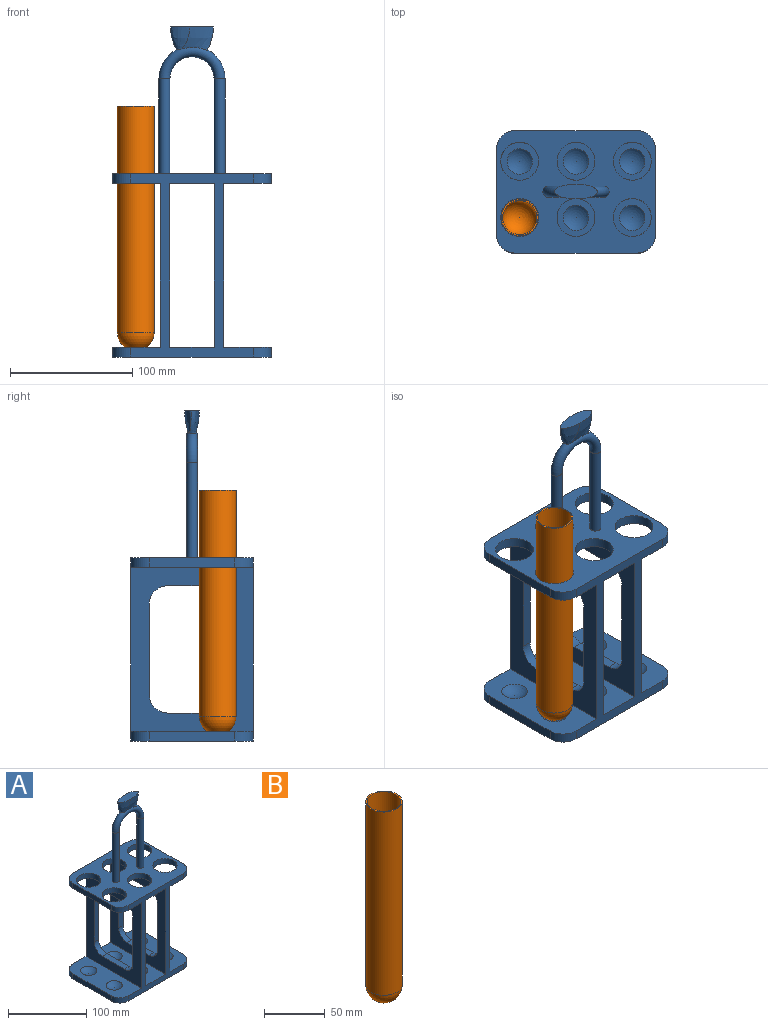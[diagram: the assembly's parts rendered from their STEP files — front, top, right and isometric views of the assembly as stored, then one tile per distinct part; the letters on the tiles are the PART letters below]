
ASSEMBLY  parts=2 mates=1
PART A: 62 faces, bbox 130.6x100.6x270.6 mm
  f0: plane 130x100mm, normal (0,0,1), area 8151mm2, adj f1,f3,f5,f7,f9,f15,f16,f26
  f1: cylinder r=15.5mm len=31mm, axis (0,0,-1), area 779.1mm2, adj f0,f25
  f2: sphere r=15.5mm, area 389.6mm2, adj f22
  f3: cylinder r=15.5mm len=31mm, axis (0,0,-1), area 779.1mm2, adj f0,f23
  f4: sphere r=15.5mm, area 389.6mm2, adj f24
  f5: cylinder r=15.5mm len=31mm, axis (0,0,-1), area 779.1mm2, adj f0,f17
  f6: sphere r=15.5mm, area 389.6mm2, adj f18
  f7: cylinder r=15.5mm len=31mm, axis (0,0,-1), area 779.1mm2, adj f0,f25
  f8: sphere r=15.5mm, area 389.6mm2, adj f22
  f9: cylinder r=15.5mm len=31mm, axis (0,0,-1), area 779.1mm2, adj f0,f23
  f10: sphere r=15.5mm, area 389.6mm2, adj f24
  f11: plane 134x100mm, normal (-1,0,0), area 6313.1mm2, adj f17,f18,f26,f27,f28,f29,f30,f31
  f12: plane 134x100mm, normal (1,0,0), area 6313.1mm2, adj f22,f25,f26,f27,f36,f37,f38,f39
  f13: plane 134x100mm, normal (-1,0,0), area 6313.1mm2, adj f23,f24,f26,f27,f36,f37,f38,f39
  f14: plane 134x100mm, normal (1,0,0), area 6313.1mm2, adj f23,f24,f26,f27,f28,f29,f30,f31
  f15: plane 70x8mm, normal (1,0,0), area 560mm2, adj f0,f25,f46,f50
  f16: plane 70x8mm, normal (-1,0,0), area 560mm2, adj f0,f17,f49,f53
  f17: plane 100x39mm, normal (0,0,-1), area 2293.9mm2, adj f5,f11,f16,f26,f27,f45,f49,f53
  f18: plane 100x39mm, normal (0,0,1), area 3124.8mm2, adj f6,f11,f19,f26,f27,f44,f48,f52
  f19: plane 70x8mm, normal (-1,0,0), area 560mm2, adj f18,f20,f48,f52
  f20: plane 130x100mm, normal (0,0,-1), area 12806.9mm2, adj f19,f21,f26,f27,f47,f48,f51,f52
  f21: plane 70x8mm, normal (1,0,0), area 560mm2, adj f20,f22,f47,f51
  f22: plane 100x39mm, normal (0,0,1), area 3124.8mm2, adj f2,f8,f12,f21,f26,f27,f47,f51
  f23: plane 100x36mm, normal (0,0,-1), area 2090.5mm2, adj f3,f9,f13,f14,f26,f27
  f24: plane 100x36mm, normal (0,0,1), area 2921.4mm2, adj f4,f10,f13,f14,f26,f27
  f25: plane 100x39mm, normal (0,0,-1), area 2293.9mm2, adj f1,f7,f12,f15,f26,f27,f46,f50
  f26: plane 150x100mm, normal (0,-1,0), area 3744mm2, adj f0,f11,f12,f13,f14,f17,f18,f20
  f27: plane 150x100mm, normal (0,1,0), area 3744mm2, adj f0,f11,f12,f13,f14,f17,f18,f20
  f28: cylinder r=15mm len=15mm, axis (1,0,0), area 188.5mm2, adj f11,f14,f29,f35
  f29: plane 74x8mm, normal (0,-1,0), area 592mm2, adj f11,f14,f28,f30
  f30: cylinder r=15mm len=15mm, axis (1,0,0), area 188.5mm2, adj f11,f14,f29,f31
  f31: plane 40x8mm, normal (0,0,1), area 320mm2, adj f11,f14,f30,f32
  f32: cylinder r=15mm len=15mm, axis (1,0,0), area 188.5mm2, adj f11,f14,f31,f33
  f33: plane 74x8mm, normal (0,1,0), area 592mm2, adj f11,f14,f32,f34
  f34: cylinder r=15mm len=15mm, axis (1,0,0), area 188.5mm2, adj f11,f14,f33,f35
  f35: plane 40x8mm, normal (0,0,-1), area 320mm2, adj f11,f14,f28,f34
  f36: plane 40x8mm, normal (0,0,-1), area 320mm2, adj f12,f13,f37,f43
  f37: cylinder r=15mm len=15mm, axis (1,0,0), area 188.5mm2, adj f12,f13,f36,f38
  f38: plane 74x8mm, normal (0,1,0), area 592mm2, adj f12,f13,f37,f39
  f39: cylinder r=15mm len=15mm, axis (1,0,0), area 188.5mm2, adj f12,f13,f38,f40
  f40: plane 40x8mm, normal (0,0,1), area 320mm2, adj f12,f13,f39,f41
  f41: cylinder r=15mm len=15mm, axis (1,0,0), area 188.5mm2, adj f12,f13,f40,f42
  f42: plane 74x8mm, normal (0,-1,0), area 592mm2, adj f12,f13,f41,f43
  f43: cylinder r=15mm len=15mm, axis (1,0,0), area 188.5mm2, adj f12,f13,f36,f42
  f44: sphere r=15.5mm, area 389.6mm2, adj f18
  f45: cylinder r=15.5mm len=31mm, axis (0,0,-1), area 779.1mm2, adj f0,f17
  f46: cylinder r=15mm len=15mm, axis (0,0,1), area 188.5mm2, adj f0,f15,f25,f27
  f47: cylinder r=15mm len=15mm, axis (0,0,1), area 188.5mm2, adj f20,f21,f22,f27
  f48: cylinder r=15mm len=15mm, axis (0,0,-1), area 188.5mm2, adj f18,f19,f20,f27
  f49: cylinder r=15mm len=15mm, axis (0,0,-1), area 188.5mm2, adj f0,f16,f17,f27
  f50: cylinder r=15mm len=15mm, axis (0,0,-1), area 188.5mm2, adj f0,f15,f25,f26
  f51: cylinder r=15mm len=15mm, axis (0,0,-1), area 188.5mm2, adj f20,f21,f22,f26
  f52: cylinder r=15mm len=15mm, axis (0,0,1), area 188.5mm2, adj f18,f19,f20,f26
  f53: cylinder r=15mm len=15mm, axis (0,0,1), area 188.5mm2, adj f0,f16,f17,f26
  f54: cylinder r=4.5mm len=77.5mm, axis (0,0,1), area 2191.3mm2, adj f0,f55
  f55: torus R=22.5mm, axis (0,1,0), area 1831.2mm2, adj f54,f56,f58,f59,f60,f61
  f56: cylinder r=4.5mm len=77.5mm, axis (0,0,-1), area 2191.3mm2, adj f0,f55
  f57: plane 35.64x12.62mm, normal (0,0,1), area 329.9mm2, adj f58,f59,f60,f61
  f58: bspline ~29.4x20mm, area 370.7mm2, adj f55,f57,f59,f61
  f59: bspline ~20x15.71mm, area 275.6mm2, adj f55,f57,f58,f60
  f60: bspline ~29.4x20mm, area 370.7mm2, adj f55,f57,f59,f61
  f61: bspline ~20x15.71mm, area 275.6mm2, adj f55,f57,f58,f60
PART B: 5 faces, bbox 30x30x200 mm
  f0: plane 30x30mm, normal (0,0,1), area 91.1mm2, adj f1,f3
  f1: cylinder r=15mm len=185mm, axis (0,0,-1), area 17435.8mm2, adj f0,f2
  f2: sphere r=15mm, area 1413.7mm2, adj f1
  f3: cylinder r=14mm len=185mm, axis (0,0,-1), area 16273.4mm2, adj f0,f4
  f4: sphere r=14mm, area 1231.5mm2, adj f3
PLACE A at identity fixed
PLACE B rot(axis=(0,0,1),180deg) t=(-46,-71,5)mm
MATE slider A.f5 <-> B.f1  axis (0,0,-1) through (-46,-71,150)mm
